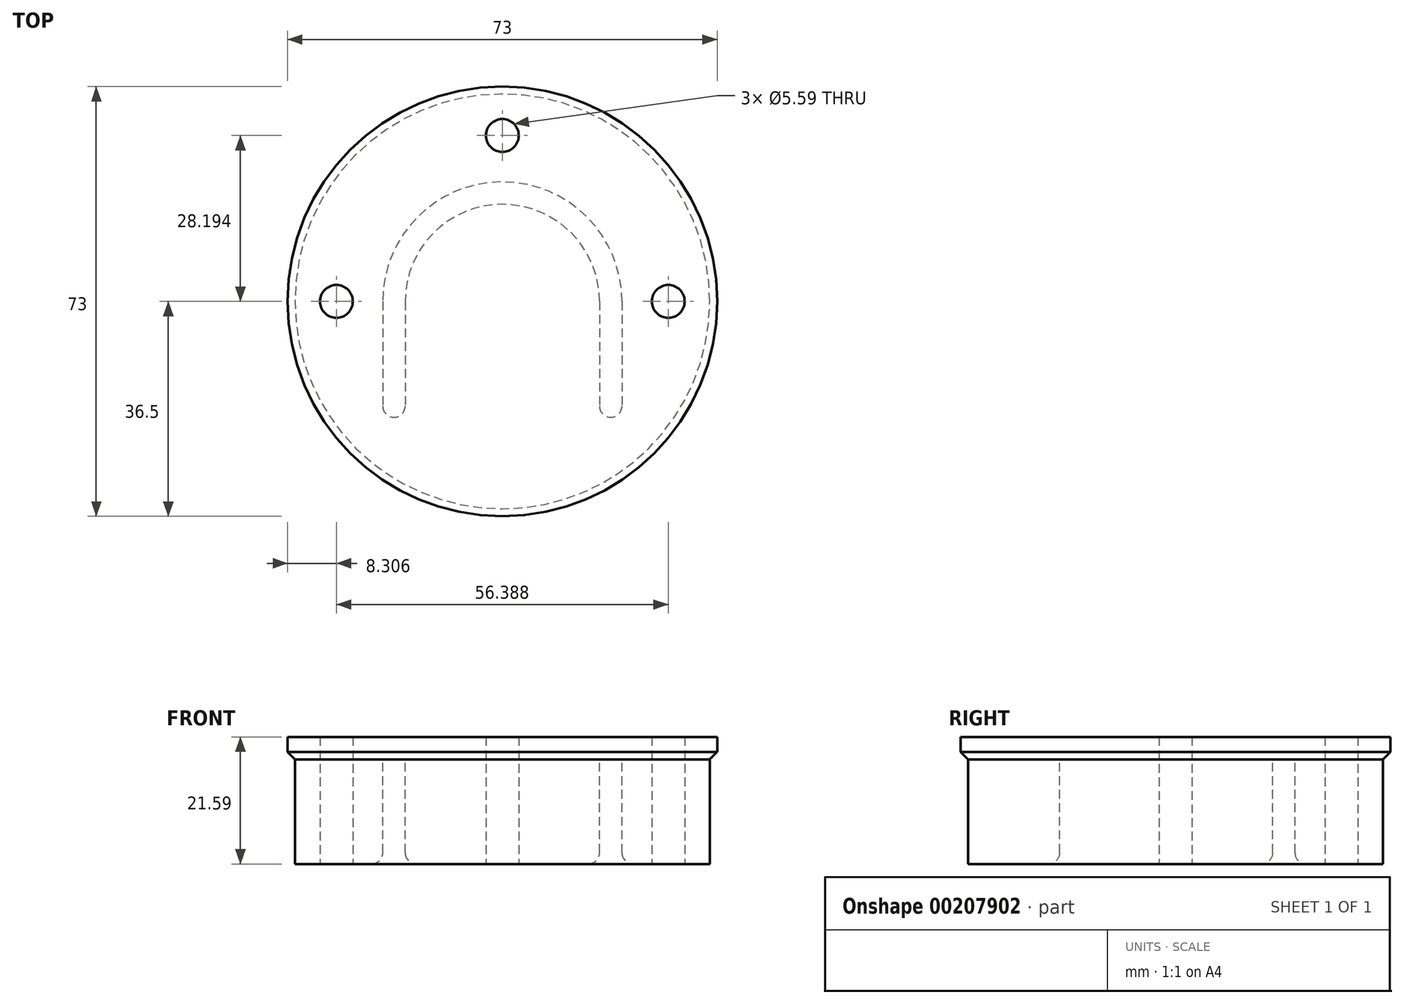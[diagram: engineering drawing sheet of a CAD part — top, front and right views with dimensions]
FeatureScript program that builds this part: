
annotation { "Feature Type Name" : "Feature", "Feature Type Description" : "" }
export const myFeature = defineFeature(function(context is Context, id is Id, definition is map)
    precondition{}
    {
        {
            var Q0;
            Q0=qCreatedBy(makeId("Top.planeOp"),FACE);
            var sketch = newSketch(context, id + "F0", { "sketchPlane" : qUnion([Q0])});
            skCircle(sketch, "E0", {"center": v(0, 0) * mm, "radius": 36.5 * mm});
            skCircle(sketch, "E1", {"center": v(0, 0) * mm, "radius": 28.2 * mm, "construction": true});
            skCircle(sketch, "E2", {"center": v(-28.2, 0) * mm, "radius": 2.8 * mm});
            skCircle(sketch, "E3", {"center": v(0, 28.2) * mm, "radius": 2.8 * mm});
            skCircle(sketch, "E4", {"center": v(28.2, 0) * mm, "radius": 2.8 * mm});
            skSolve(sketch);
        }
        {
            var Q0;
            Q0=makeQuery(id+"F0.imprint","IMPRINT",FACE,{"disambiguationData":[TD([[makeQuery(id+"F0.imprint","IMPRINT",EDGE,{"derivedFrom":sQuery(id+"F0.wireOp",EDGE,"E0")}),1.0]])]});
            extrude(context, id + "F1", {"entities" : qUnion([Q0]), "depth" : 3.8 * mm});
        }
        {
            var Q0;
            Q0=makeQuery(id+"F1.opExtrude","CAP_EDGE",EDGE,{"disambiguationData":[OSD([sQuery(id+"F0.wireOp",EDGE,"E0")])],"isStart":true});
            chamfer(context, id + "F2", {"entities" : qUnion([Q0]), "width" : 1.27 * mm, "tangentPropagation" : true});
        }
        {
            var Q0;
            Q0=makeQuery(id+"F1.opExtrude","CAP_FACE",FACE,{"disambiguationData":[OSD([sQuery(id+"F0.wireOp",EDGE,"E0"),sQuery(id+"F0.wireOp",EDGE,"E2"),sQuery(id+"F0.wireOp",EDGE,"E3"),sQuery(id+"F0.wireOp",EDGE,"E4")])],"isStart":true});
            var sketch = newSketch(context, id + "F3", { "sketchPlane" : qUnion([Q0])});
            skArc(sketch, "E5", {"start": v(16.51, 0) * mm, "mid": v(0, -16.51) * mm, "end": v(-16.51, 0) * mm});
            skLineSegment(sketch, "E6", {"start": v(-16.51, 0) * mm, "end": v(-16.51, 17.78) * mm});
            skLineSegment(sketch, "E7", {"start": v(16.51, 0) * mm, "end": v(16.51, 17.78) * mm});
            skLineSegment(sketch, "E8.0", {"start": v(-20.32, 0) * mm, "end": v(-20.32, 17.78) * mm});
            skArc(sketch, "E8.1", {"start": v(20.32, 0) * mm, "mid": v(0, -20.32) * mm, "end": v(-20.32, 0) * mm});
            skLineSegment(sketch, "E8.2", {"start": v(20.32, 0) * mm, "end": v(20.32, 17.78) * mm});
            skArc(sketch, "E9", {"start": v(-20.32, 17.78) * mm, "mid": v(-18.42, 19.69) * mm, "end": v(-16.51, 17.78) * mm});
            skArc(sketch, "E10", {"start": v(16.51, 17.78) * mm, "mid": v(18.41, 19.69) * mm, "end": v(20.32, 17.78) * mm});
            skSolve(sketch);
        }
        {
            var Q0;
            Q0=makeQuery(id+"F3.imprint","IMPRINT",FACE,{"disambiguationData":[TD([[makeQuery(id+"F3.imprint","IMPRINT",EDGE,{"derivedFrom":sQuery(id+"F3.wireOp",EDGE,"E5")}),1.0]])]});
            extrude(context, id + "F4", {"entities" : qUnion([Q0]), "operationType" : NewBodyOperationType.ADD, "depth" : 17.78 * mm});
        }
        {
            var Q0;
            Q0=makeQuery(id+"F4.opExtrude","CAP_EDGE",EDGE,{"disambiguationData":[OSD([sQuery(id+"F3.wireOp",EDGE,"E8.0")])],"isStart":false});
            var Q1;
            Q1=makeQuery(id+"F4.opExtrude","CAP_EDGE",EDGE,{"disambiguationData":[OSD([sQuery(id+"F3.wireOp",EDGE,"E6")])],"isStart":false});
            var Q2;
            Q2=makeQuery(id+"F4.opExtrude","CAP_EDGE",EDGE,{"disambiguationData":[OSD([sQuery(id+"F3.wireOp",EDGE,"E9")])],"isStart":false});
            var Q3;
            Q3=makeQuery(id+"F4.opExtrude","CAP_EDGE",EDGE,{"disambiguationData":[OSD([sQuery(id+"F3.wireOp",EDGE,"E8.1")])],"isStart":false});
            var Q4;
            Q4=makeQuery(id+"F4.opExtrude","CAP_EDGE",EDGE,{"disambiguationData":[OSD([sQuery(id+"F3.wireOp",EDGE,"E5")])],"isStart":false});
            var Q5;
            Q5=makeQuery(id+"F4.opExtrude","CAP_EDGE",EDGE,{"disambiguationData":[OSD([sQuery(id+"F3.wireOp",EDGE,"E7")])],"isStart":false});
            var Q6;
            Q6=makeQuery(id+"F4.opExtrude","CAP_EDGE",EDGE,{"disambiguationData":[OSD([sQuery(id+"F3.wireOp",EDGE,"E8.2")])],"isStart":false});
            var Q7;
            Q7=makeQuery(id+"F4.opExtrude","CAP_EDGE",EDGE,{"disambiguationData":[OSD([sQuery(id+"F3.wireOp",EDGE,"E10")])],"isStart":false});
            fillet(context, id + "F5", {"entities" : qUnion([Q0, Q1, Q2, Q3, Q4, Q5, Q6, Q7]), "radius" : 1.9 * mm, "tangentPropagation" : true, "allowEdgeOverflow" : false});
        }
    });
